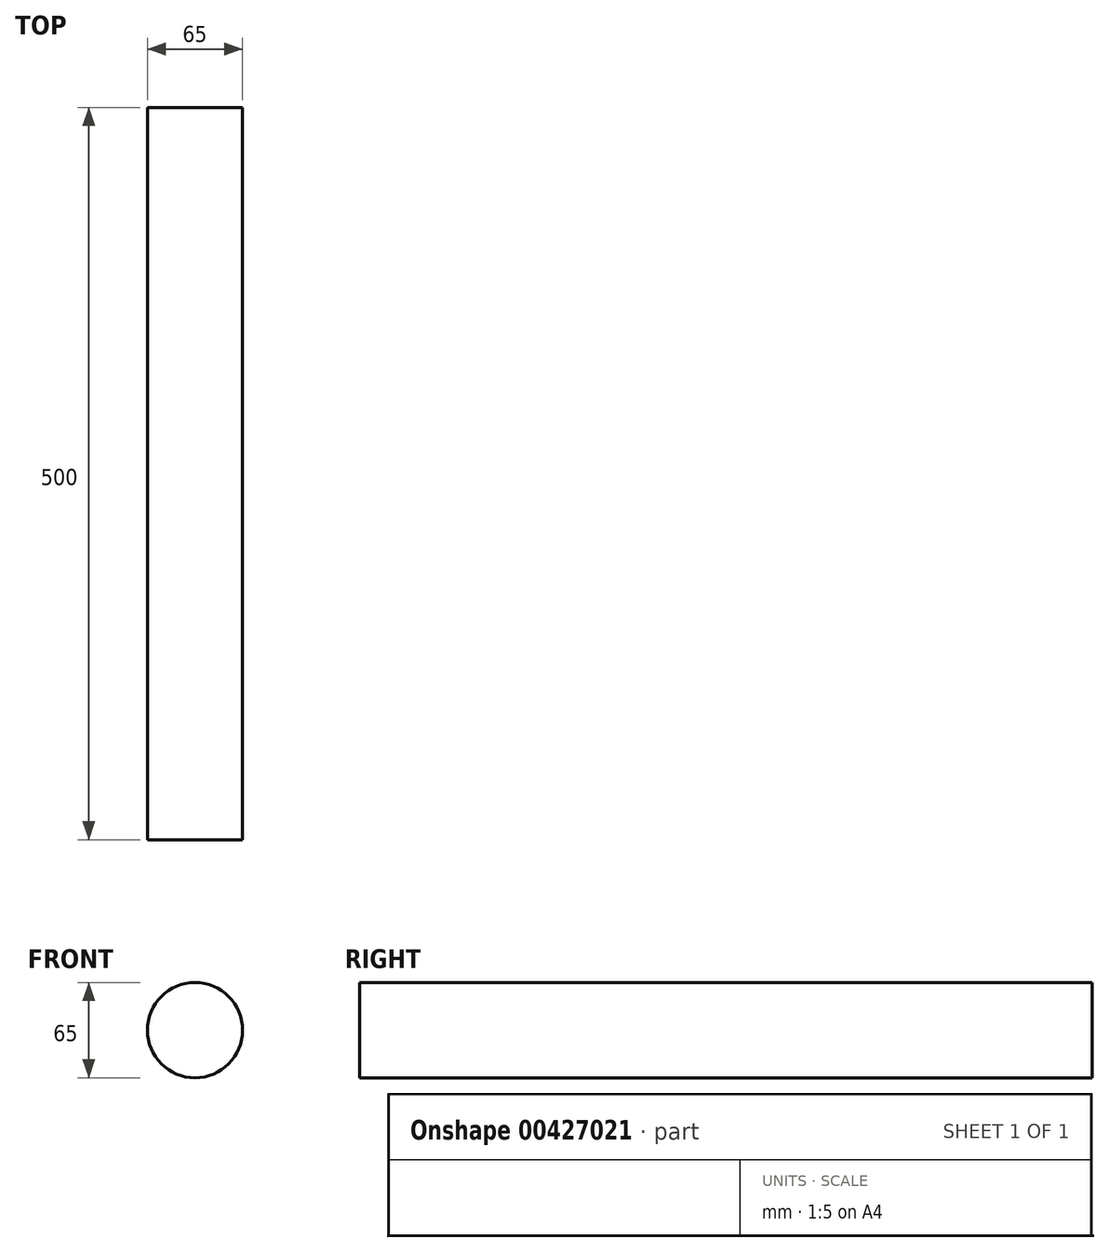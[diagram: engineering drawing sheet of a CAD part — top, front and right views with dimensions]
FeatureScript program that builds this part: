
annotation { "Feature Type Name" : "Feature", "Feature Type Description" : "" }
export const myFeature = defineFeature(function(context is Context, id is Id, definition is map)
    precondition{}
    {
        {
            var Q0;
            Q0=qCreatedBy(makeId("Front.planeOp"),FACE);
            var sketch = newSketch(context, id + "F0", { "sketchPlane" : qUnion([Q0])});
            skCircle(sketch, "E0", {"center": v(0, 0) * mm, "radius": 32.5 * mm});
            skSolve(sketch);
        }
        {
            var Q0;
            Q0 = qSketchRegion(id + "F0", true);
            extrude(context, id + "F1", {"entities" : qUnion([Q0]), "endBound" : BoundingType.SYMMETRIC, "depth" : 500 * mm});
        }
    });
